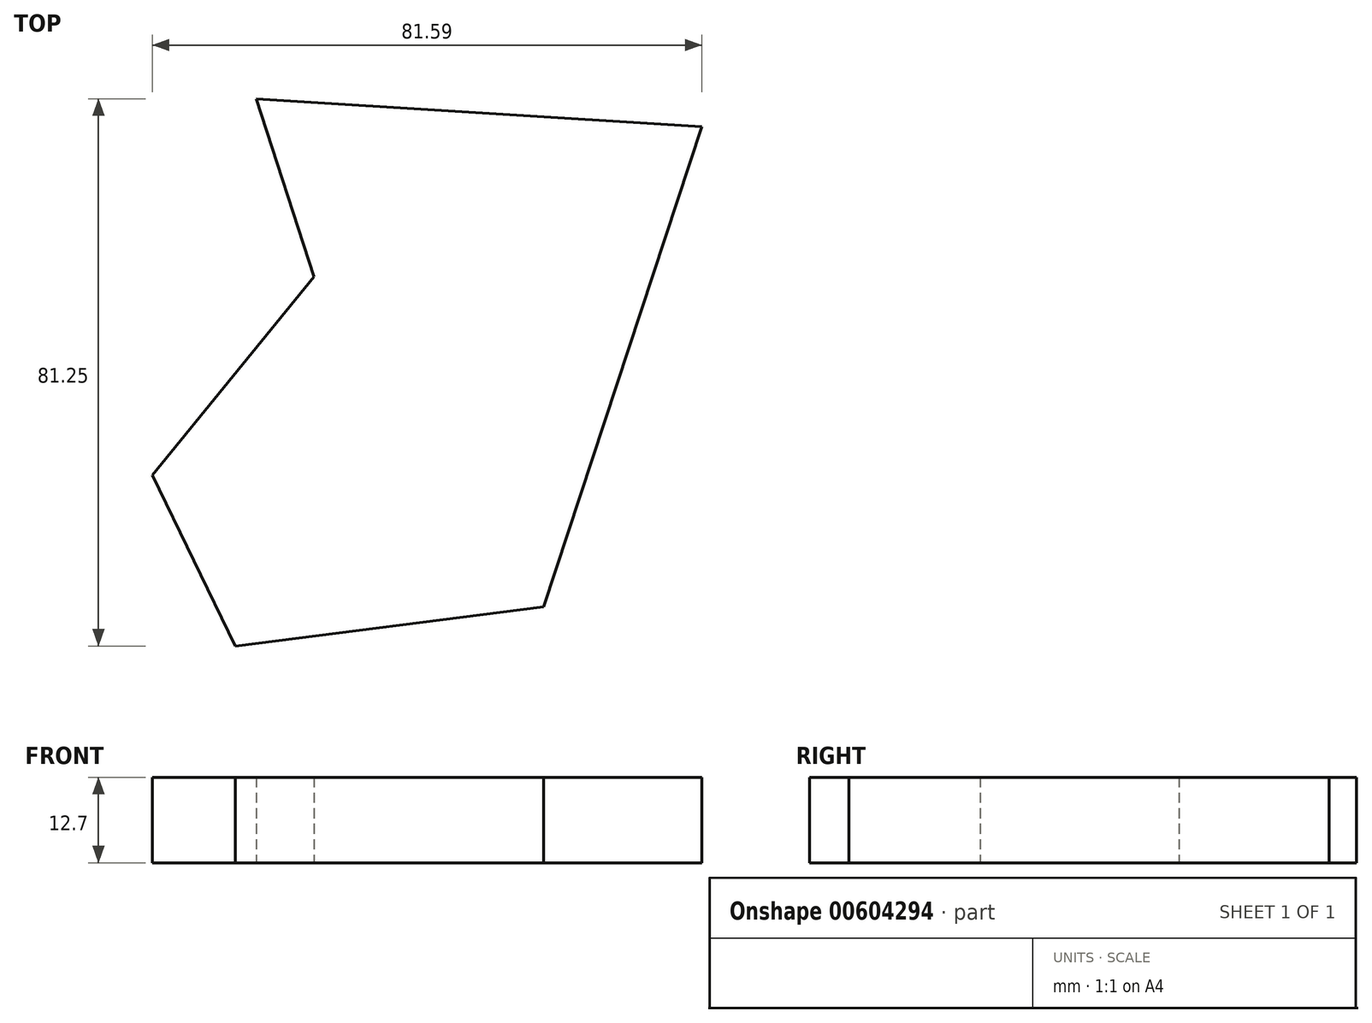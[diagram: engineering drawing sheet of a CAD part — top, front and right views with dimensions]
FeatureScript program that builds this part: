
annotation { "Feature Type Name" : "Feature", "Feature Type Description" : "" }
export const myFeature = defineFeature(function(context is Context, id is Id, definition is map)
    precondition{}
    {
        {
            var Q0;
            Q0=qCreatedBy(makeId("Top.planeOp"),FACE);
            var sketch = newSketch(context, id + "F0", { "sketchPlane" : qUnion([Q0])});
            skLineSegment(sketch, "E0", {"start": v(-58.11, 0) * mm, "end": v(-34.11, 29.48) * mm});
            skLineSegment(sketch, "E1", {"start": v(-34.11, 29.48) * mm, "end": v(-42.68, 55.88) * mm});
            skLineSegment(sketch, "E2", {"start": v(-42.68, 55.88) * mm, "end": v(23.48, 51.77) * mm});
            skLineSegment(sketch, "E3", {"start": v(23.48, 51.77) * mm, "end": v(0, -19.54) * mm});
            skLineSegment(sketch, "E4", {"start": v(0, -19.54) * mm, "end": v(-45.77, -25.37) * mm});
            skLineSegment(sketch, "E5", {"start": v(-45.77, -25.37) * mm, "end": v(-58.11, 0) * mm});
            skSolve(sketch);
        }
        {
            var Q0;
            Q0=makeQuery(id+"F0.imprint","IMPRINT",FACE,{"disambiguationData":[TD([[makeQuery(id+"F0.imprint","IMPRINT",EDGE,{"derivedFrom":sQuery(id+"F0.wireOp",EDGE,"E0")}),-1.0]])]});
            extrude(context, id + "F1", {"entities" : qUnion([Q0]), "depth" : 12.7 * mm, "offsetDistance" : 25.4 * mm});
        }
    });
